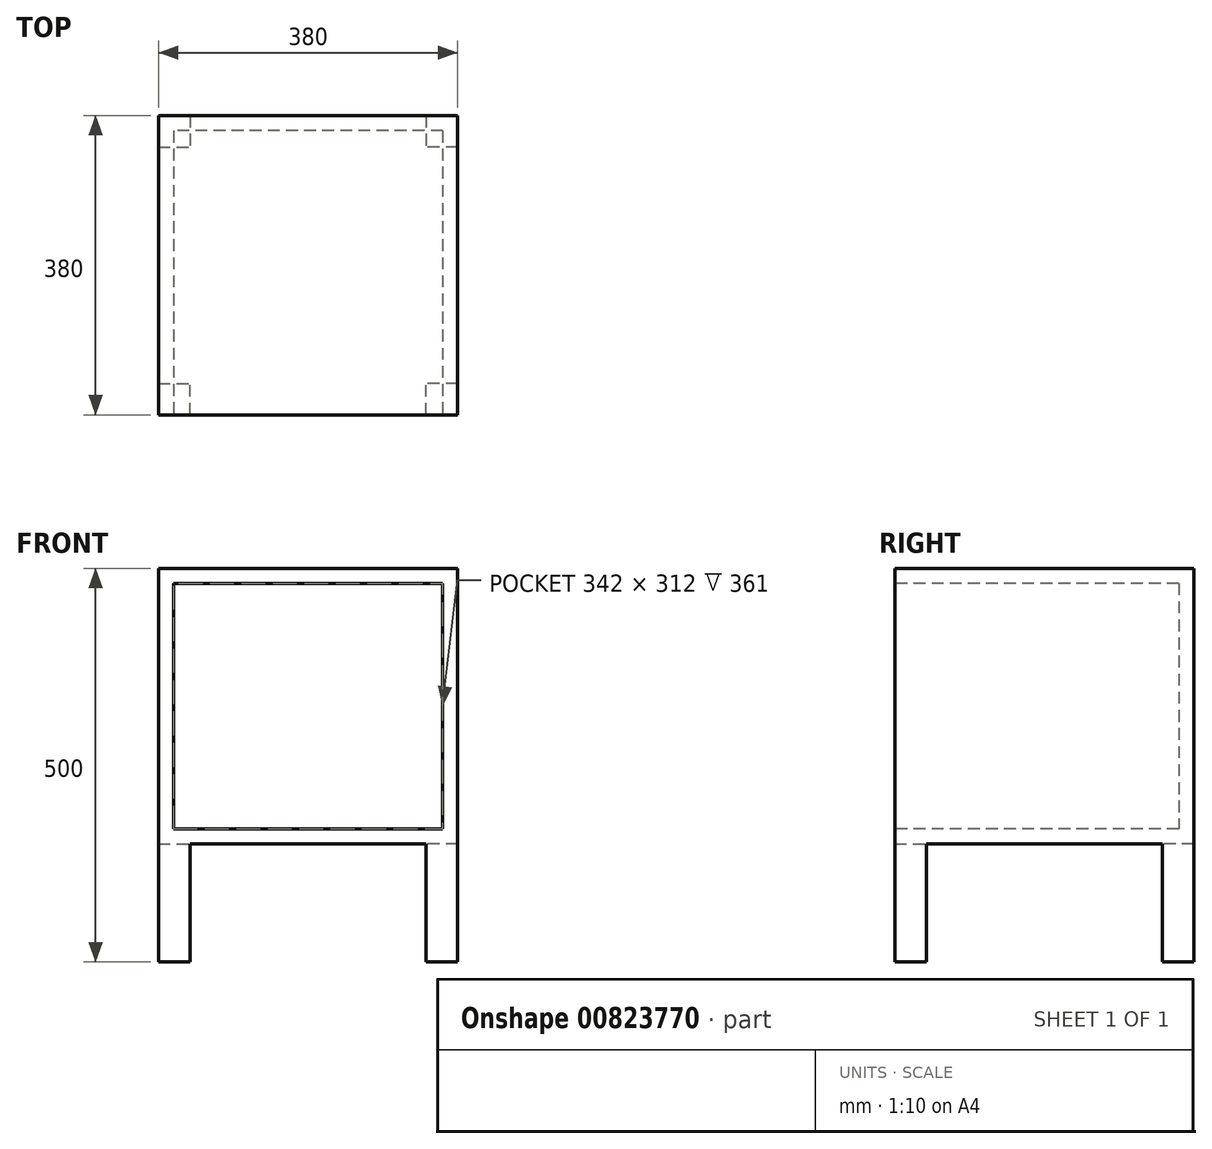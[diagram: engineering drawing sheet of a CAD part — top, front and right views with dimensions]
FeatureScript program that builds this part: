
annotation { "Feature Type Name" : "Feature", "Feature Type Description" : "" }
export const myFeature = defineFeature(function(context is Context, id is Id, definition is map)
    precondition{}
    {
        {
            var Q0;
            Q0=qCreatedBy(makeId("Top.planeOp"),FACE);
            var sketch = newSketch(context, id + "F0", { "sketchPlane" : qUnion([Q0])});
            skLineSegment(sketch, "E0.bottom", {"start": v(190, -190) * mm, "end": v(-190, -190) * mm});
            skLineSegment(sketch, "E0.top", {"start": v(190, 190) * mm, "end": v(-190, 190) * mm});
            skLineSegment(sketch, "E0.left", {"start": v(190, -190) * mm, "end": v(190, 190) * mm});
            skLineSegment(sketch, "E0.right", {"start": v(-190, -190) * mm, "end": v(-190, 190) * mm});
            skPoint(sketch, "E0.middle", {"position": v(0, 0) * mm});
            skSolve(sketch);
        }
        {
            var Q0;
            Q0=makeQuery(id+"F0.imprint","IMPRINT",FACE,{"disambiguationData":[TD([[makeQuery(id+"F0.imprint","IMPRINT",EDGE,{"derivedFrom":sQuery(id+"F0.wireOp",EDGE,"E0.bottom")}),-1.0]])]});
            extrude(context, id + "F1", {"entities" : qUnion([Q0]), "depth" : 350 * mm, "offsetDistance" : 25 * mm});
        }
        {
            var Q0;
            Q0=makeQuery(id+"F1.opExtrude","SWEPT_FACE",FACE,{"disambiguationData":[OSD([sQuery(id+"F0.wireOp",EDGE,"E0.bottom")])]});
            var sketch = newSketch(context, id + "F2", { "sketchPlane" : qUnion([Q0])});
            skLineSegment(sketch, "E1.bottom", {"start": v(171, 331) * mm, "end": v(-171, 331) * mm});
            skLineSegment(sketch, "E1.top", {"start": v(171, 19) * mm, "end": v(-171, 19) * mm});
            skLineSegment(sketch, "E1.left", {"start": v(171, 331) * mm, "end": v(171, 19) * mm});
            skLineSegment(sketch, "E1.right", {"start": v(-171, 331) * mm, "end": v(-171, 19) * mm});
            skPoint(sketch, "E1.middle", {"position": v(0, 175) * mm});
            skSolve(sketch);
        }
        {
            var Q0;
            Q0=makeQuery(id+"F2.imprint","IMPRINT",FACE,{"disambiguationData":[TD([[makeQuery(id+"F2.imprint","IMPRINT",EDGE,{"derivedFrom":sQuery(id+"F2.wireOp",EDGE,"E1.bottom")}),1.0]])]});
            extrude(context, id + "F3", {"entities" : qUnion([Q0]), "operationType" : NewBodyOperationType.REMOVE, "oppositeDirection" : true, "depth" : 361 * mm, "offsetDistance" : 25 * mm});
        }
        {
            var Q0;
            Q0=makeQuery(id+"F1.opExtrude","CAP_FACE",FACE,{"disambiguationData":[OSD([sQuery(id+"F0.wireOp",EDGE,"E0.bottom"),sQuery(id+"F0.wireOp",EDGE,"E0.top"),sQuery(id+"F0.wireOp",EDGE,"E0.left"),sQuery(id+"F0.wireOp",EDGE,"E0.right")])],"isStart":true});
            var sketch = newSketch(context, id + "F4", { "sketchPlane" : qUnion([Q0])});
            skLineSegment(sketch, "E2.bottom", {"start": v(190, 190) * mm, "end": v(150, 190) * mm});
            skLineSegment(sketch, "E2.top", {"start": v(190, 150) * mm, "end": v(150, 150) * mm});
            skLineSegment(sketch, "E2.left", {"start": v(190, 190) * mm, "end": v(190, 150) * mm});
            skLineSegment(sketch, "E2.right", {"start": v(150, 190) * mm, "end": v(150, 150) * mm});
            skLineSegment(sketch, "E3.bottom", {"start": v(-190, 190) * mm, "end": v(-150, 190) * mm});
            skLineSegment(sketch, "E3.top", {"start": v(-190, 150) * mm, "end": v(-150, 150) * mm});
            skLineSegment(sketch, "E3.left", {"start": v(-190, 190) * mm, "end": v(-190, 150) * mm});
            skLineSegment(sketch, "E3.right", {"start": v(-150, 190) * mm, "end": v(-150, 150) * mm});
            skLineSegment(sketch, "E4.bottom", {"start": v(-190, -190) * mm, "end": v(-150, -190) * mm});
            skLineSegment(sketch, "E4.top", {"start": v(-190, -150) * mm, "end": v(-150, -150) * mm});
            skLineSegment(sketch, "E4.left", {"start": v(-190, -190) * mm, "end": v(-190, -150) * mm});
            skLineSegment(sketch, "E4.right", {"start": v(-150, -190) * mm, "end": v(-150, -150) * mm});
            skLineSegment(sketch, "E5.bottom", {"start": v(190, -190) * mm, "end": v(150, -190) * mm});
            skLineSegment(sketch, "E5.top", {"start": v(190, -150) * mm, "end": v(150, -150) * mm});
            skLineSegment(sketch, "E5.left", {"start": v(190, -190) * mm, "end": v(190, -150) * mm});
            skLineSegment(sketch, "E5.right", {"start": v(150, -190) * mm, "end": v(150, -150) * mm});
            skSolve(sketch);
        }
        {
            var Q0;
            Q0=makeQuery(id+"F4.imprint","IMPRINT",FACE,{"disambiguationData":[TD([[makeQuery(id+"F4.imprint","IMPRINT",EDGE,{"derivedFrom":sQuery(id+"F4.wireOp",EDGE,"E2.bottom")}),1.0]])]});
            var Q1;
            Q1=makeQuery(id+"F4.imprint","IMPRINT",FACE,{"disambiguationData":[TD([[makeQuery(id+"F4.imprint","IMPRINT",EDGE,{"derivedFrom":sQuery(id+"F4.wireOp",EDGE,"E3.bottom")}),1.0]])]});
            var Q2;
            Q2=makeQuery(id+"F4.imprint","IMPRINT",FACE,{"disambiguationData":[TD([[makeQuery(id+"F4.imprint","IMPRINT",EDGE,{"derivedFrom":sQuery(id+"F4.wireOp",EDGE,"E4.bottom")}),-1.0]])]});
            var Q3;
            Q3=makeQuery(id+"F4.imprint","IMPRINT",FACE,{"disambiguationData":[TD([[makeQuery(id+"F4.imprint","IMPRINT",EDGE,{"derivedFrom":sQuery(id+"F4.wireOp",EDGE,"E5.bottom")}),-1.0]])]});
            extrude(context, id + "F5", {"entities" : qUnion([Q0, Q1, Q2, Q3]), "operationType" : NewBodyOperationType.ADD, "depth" : 150 * mm, "offsetDistance" : 25 * mm});
        }
    });
